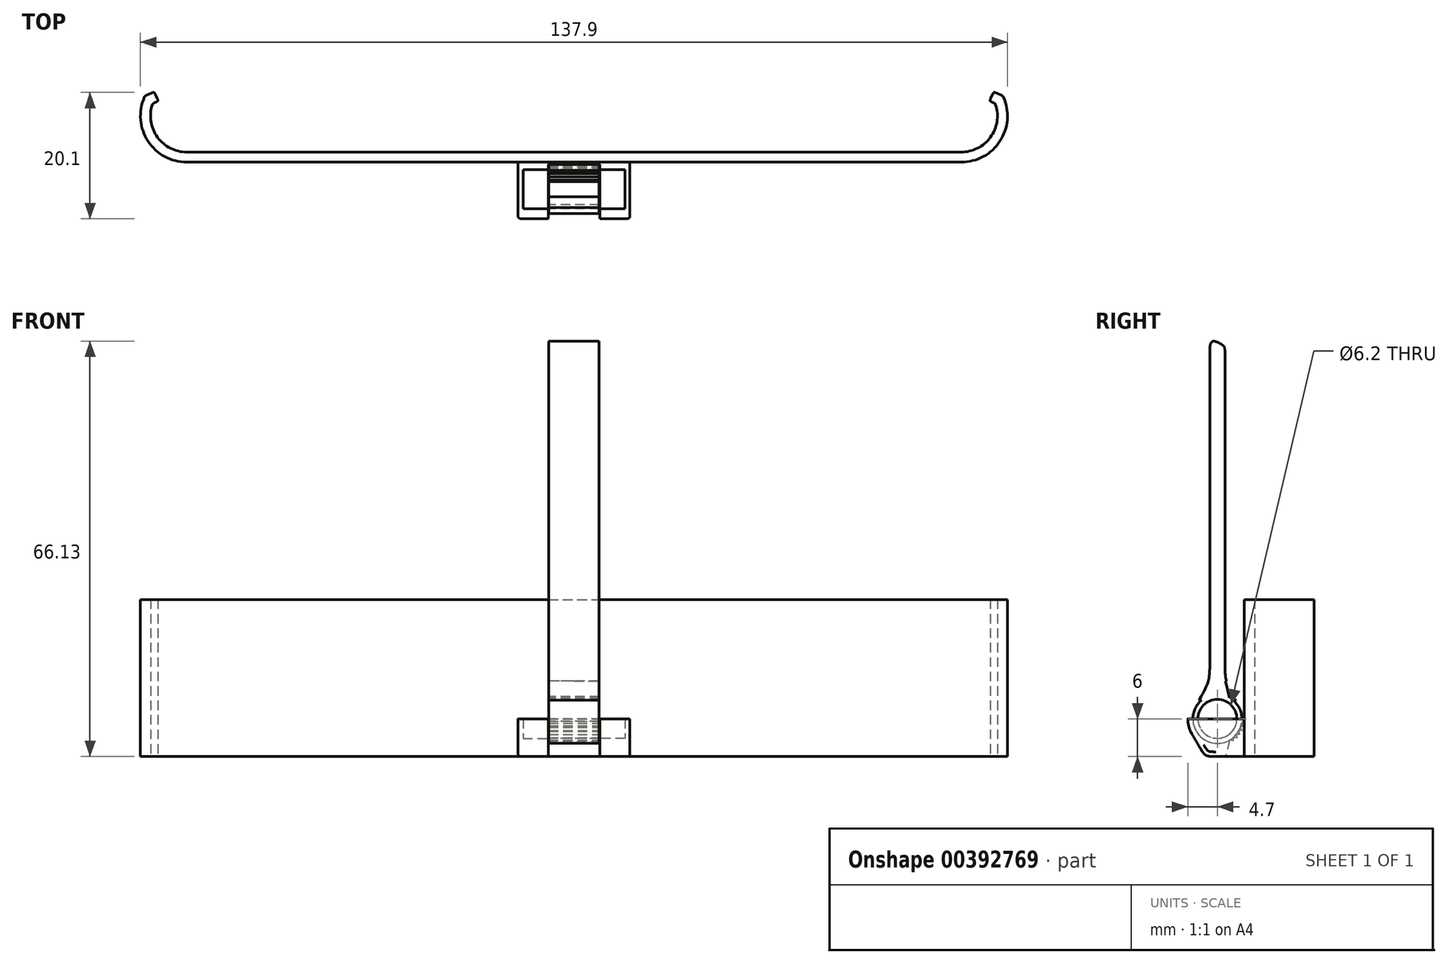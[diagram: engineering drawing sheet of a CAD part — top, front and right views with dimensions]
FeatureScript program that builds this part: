
annotation { "Feature Type Name" : "Feature", "Feature Type Description" : "" }
export const myFeature = defineFeature(function(context is Context, id is Id, definition is map)
    precondition{}
    {
        {
            var Q0;
            Q0=qCreatedBy(makeId("Top.planeOp"),FACE);
            var sketch = newSketch(context, id + "F0", { "sketchPlane" : qUnion([Q0])});
            skLineSegment(sketch, "E0", {"start": v(0, 0) * mm, "end": v(61.6, 0) * mm});
            skLineSegment(sketch, "E1", {"start": v(67, 7.72) * mm, "end": v(66.1, 8.14) * mm});
            skArc(sketch, "E2", {"start": v(61.6, 0) * mm, "mid": v(66.3, 2.45) * mm, "end": v(67, 7.72) * mm});
            skLineSegment(sketch, "E3", {"start": v(61.6, 5.75) * mm, "end": v(67, 7.72) * mm, "construction": true});
            skLineSegment(sketch, "E4", {"start": v(67, 7.72) * mm, "end": v(65.65, 11.43) * mm, "construction": true});
            skLineSegment(sketch, "E5", {"start": v(0, 0) * mm, "end": v(0, -1.6) * mm});
            skLineSegment(sketch, "E6", {"start": v(0, -1.6) * mm, "end": v(61.6, -1.6) * mm});
            skArc(sketch, "E7", {"start": v(61.6, -1.6) * mm, "mid": v(67.81, 1.82) * mm, "end": v(68.23, 8.9) * mm});
            skLineSegment(sketch, "E8", {"start": v(68.23, 8.9) * mm, "end": v(66.77, 9.59) * mm});
            skLineSegment(sketch, "E9", {"start": v(66.77, 9.59) * mm, "end": v(66.1, 8.14) * mm});
            skSolve(sketch);
        }
        {
            var Q0;
            Q0 = qSketchRegion(id + "F0", true);
            extrude(context, id + "F1", {"entities" : qUnion([Q0]), "endBound" : BoundingType.SYMMETRIC, "depth" : 25 * mm});
        }
        {
            var Q0;
            Q0=makeQuery(id+"F1.opExtrude","SWEPT_EDGE",EDGE,{"disambiguationData":[OSD([sQuery(id+"F0.wireOp",EDGE,"E1"),sQuery(id+"F0.wireOp",EDGE,"E2")])]});
            var Q1;
            Q1=makeQuery(id+"F1.opExtrude","SWEPT_EDGE",EDGE,{"disambiguationData":[OSD([sQuery(id+"F0.wireOp",EDGE,"E1"),sQuery(id+"F0.wireOp",EDGE,"E9")])]});
            var Q2;
            Q2=makeQuery(id+"F1.opExtrude","SWEPT_EDGE",EDGE,{"disambiguationData":[OSD([sQuery(id+"F0.wireOp",EDGE,"E8"),sQuery(id+"F0.wireOp",EDGE,"E9")])]});
            var Q3;
            Q3=makeQuery(id+"F1.opExtrude","SWEPT_EDGE",EDGE,{"disambiguationData":[OSD([sQuery(id+"F0.wireOp",EDGE,"E7"),sQuery(id+"F0.wireOp",EDGE,"E8")])]});
            fillet(context, id + "F2", {"entities" : qUnion([Q0, Q1, Q2, Q3]), "radius" : .5 * mm, "tangentPropagation" : true, "rho" : .7, "crossSection" : FilletCrossSection.CONIC, "allowEdgeOverflow" : false});
        }
        {
            var Q0;
            Q0=qCreatedBy(makeId("Right.planeOp"),FACE);
            cPlane(context, id + "F3", {"entities" : qUnion([Q0]), "cplaneType" : CPlaneType.OFFSET, "offset" : 4.1 * mm, "width" : 150 * mm, "height" : 150 * mm});
        }
        {
            var Q0;
            Q0=qCreatedBy(id+"F3.planeOp",FACE);
            var sketch = newSketch(context, id + "F4", { "sketchPlane" : qUnion([Q0])});
            skLineSegment(sketch, "E10", {"start": v(-7.86, -12.5) * mm, "end": v(-9.97, -8.85) * mm});
            skArc(sketch, "E11", {"start": v(-10.6, -6.5) * mm, "mid": v(-10.44, -7.72) * mm, "end": v(-9.97, -8.85) * mm});
            skArc(sketch, "E12", {"start": v(-9, -6.5) * mm, "mid": v(-5.9, -9.6) * mm, "end": v(-2.8, -6.5) * mm});
            skLineSegment(sketch, "E13", {"start": v(-2.8, -6.5) * mm, "end": v(-1.6, -6.5) * mm});
            skLineSegment(sketch, "E14", {"start": v(-1.6, -6.5) * mm, "end": v(-1.6, -12.5) * mm});
            skLineSegment(sketch, "E15", {"start": v(-9, -6.5) * mm, "end": v(-10.6, -6.5) * mm});
            skLineSegment(sketch, "E16", {"start": v(-1.6, -12.5) * mm, "end": v(-7.86, -12.5) * mm});
            skSolve(sketch);
        }
        {
            var Q0;
            Q0 = qSketchRegion(id + "F4", true);
            extrude(context, id + "F5", {"entities" : qUnion([Q0]), "operationType" : NewBodyOperationType.ADD, "depth" : 4 * mm});
        }
        {
            var Q0;
            Q0=makeQuery(id+"F5.opExtrude","CAP_FACE",FACE,{"disambiguationData":[OSD([sQuery(id+"F4.wireOp",EDGE,"pzVoG1jN-wFmN-uIL8-jvUG-rm5sUtAQ56AL"),sQuery(id+"F4.wireOp",EDGE,"E10"),sQuery(id+"F4.wireOp",EDGE,"E11"),sQuery(id+"F4.wireOp",EDGE,"f0MZyzKJ-CONF-h5lc-jCnh-KOTXd5ug3wsI"),sQuery(id+"F4.wireOp",EDGE,"E12"),sQuery(id+"F4.wireOp",EDGE,"E13")])],"isStart":true});
            var sketch = newSketch(context, id + "F6", { "sketchPlane" : qUnion([Q0])});
            skLineSegment(sketch, "E17", {"start": v(1.6, -6.5) * mm, "end": v(1.6, -12.5) * mm});
            skLineSegment(sketch, "E18", {"start": v(1.75, -23.1) * mm, "end": v(1.75, -7.61) * mm, "construction": true});
            skLineSegment(sketch, "E19", {"start": v(1.75, -7.61) * mm, "end": v(2.06, -7.18) * mm});
            skLineSegment(sketch, "E20", {"start": v(2.06, -7.18) * mm, "end": v(1.62, -6.87) * mm});
            skLineSegment(sketch, "E21", {"start": v(1.62, -6.87) * mm, "end": v(2, -6.5) * mm});
            skLineSegment(sketch, "E22", {"start": v(2, -6.5) * mm, "end": v(1.6, -6.5) * mm});
            skCircle(sketch, "E23", {"center": v(5.9, -6.5) * mm, "radius": 4.3 * mm, "construction": true});
            skLineSegment(sketch, "E24", {"start": v(2, -6.5) * mm, "end": v(5.9, -6.5) * mm, "construction": true});
            skCircle(sketch, "E25", {"center": v(5.9, -6.5) * mm, "radius": 3.9 * mm, "construction": true});
            skLineSegment(sketch, "E26", {"start": v(4.62, -12.5) * mm, "end": v(1.6, -12.5) * mm});
            skLineSegment(sketch, "E27", {"start": v(1.6, -12.5) * mm, "end": v(1.6, -6.5) * mm});
            skLineSegment(sketch, "E28", {"start": v(5.9, -6.5) * mm, "end": v(2.06, -7.18) * mm, "construction": true});
            skLineSegment(sketch, "E29", {"start": v(1.75, -7.61) * mm, "end": v(2.24, -7.83) * mm});
            skLineSegment(sketch, "E30", {"start": v(2.24, -7.83) * mm, "end": v(2, -8.32) * mm});
            skLineSegment(sketch, "E31", {"start": v(2, -8.32) * mm, "end": v(2.52, -8.45) * mm});
            skLineSegment(sketch, "E32", {"start": v(2.52, -8.45) * mm, "end": v(2.38, -8.97) * mm});
            skLineSegment(sketch, "E33", {"start": v(2.38, -8.97) * mm, "end": v(2.91, -9) * mm});
            skLineSegment(sketch, "E34", {"start": v(2.91, -9) * mm, "end": v(2.86, -9.54) * mm});
            skLineSegment(sketch, "E35", {"start": v(2.86, -9.54) * mm, "end": v(3.4, -9.49) * mm});
            skLineSegment(sketch, "E36", {"start": v(3.4, -9.49) * mm, "end": v(3.43, -10.02) * mm});
            skLineSegment(sketch, "E37", {"start": v(3.43, -10.02) * mm, "end": v(3.95, -9.88) * mm});
            skLineSegment(sketch, "E38", {"start": v(3.95, -9.88) * mm, "end": v(4.08, -10.4) * mm});
            skLineSegment(sketch, "E39", {"start": v(4.08, -10.4) * mm, "end": v(4.62, -12.5) * mm});
            skSolve(sketch);
        }
        {
            var Q0;
            Q0 = qSketchRegion(id + "F6", true);
            var Q1;
            Q1=qCreatedBy(makeId("Origin.pointOp"),VERTEX);
            extrude(context, id + "F7", {"entities" : qUnion([Q0]), "operationType" : NewBodyOperationType.ADD, "endBound" : BoundingType.UP_TO_VERTEX, "endBoundEntityVertex" : qUnion([Q1]), "depth" : 4 * mm});
        }
        {
            var Q0;
            Q0=makeQuery(id+"F5.opExtrude","CAP_FACE",FACE,{"disambiguationData":[OSD([sQuery(id+"F4.wireOp",EDGE,"E10"),sQuery(id+"F4.wireOp",EDGE,"E11"),sQuery(id+"F4.wireOp",EDGE,"E12"),sQuery(id+"F4.wireOp",EDGE,"E13"),sQuery(id+"F4.wireOp",EDGE,"E14"),sQuery(id+"F4.wireOp",EDGE,"E15"),sQuery(id+"F4.wireOp",EDGE,"E16")])],"isStart":false});
            var sketch = newSketch(context, id + "F8", { "sketchPlane" : qUnion([Q0])});
            skLineSegment(sketch, "E40.0.0", {"start": v(-1.6, -12.5) * mm, "end": v(-1.6, -6.5) * mm});
            skLineSegment(sketch, "E40.0.1", {"start": v(-1.6, -6.5) * mm, "end": v(-2.8, -6.5) * mm});
            skLineSegment(sketch, "E40.0.3", {"start": v(-9, -6.5) * mm, "end": v(-10.6, -6.5) * mm});
            skArc(sketch, "E40.0.4", {"start": v(-10.6, -6.5) * mm, "mid": v(-10.44, -7.72) * mm, "end": v(-9.97, -8.85) * mm});
            skLineSegment(sketch, "E40.0.5", {"start": v(-9.97, -8.85) * mm, "end": v(-7.86, -12.5) * mm});
            skLineSegment(sketch, "E40.0.6", {"start": v(-7.86, -12.5) * mm, "end": v(-1.6, -12.5) * mm});
            skLineSegment(sketch, "E41", {"start": v(-9, -6.5) * mm, "end": v(-2.8, -6.5) * mm});
            skSolve(sketch);
        }
        {
            var Q0;
            Q0 = qSketchRegion(id + "F8", true);
            extrude(context, id + "F9", {"entities" : qUnion([Q0]), "operationType" : NewBodyOperationType.ADD, "depth" : .8 * mm});
        }
        {
            var Q0;
            Q0=qCreatedBy(makeId("Right.planeOp"),FACE);
            var sketch = newSketch(context, id + "F10", { "sketchPlane" : qUnion([Q0])});
            skCircle(sketch, "E42", {"center": v(-5.9, -6.5) * mm, "radius": 3.1 * mm});
            skPoint(sketch, "E43.center", {"position": v(0, -4.1) * mm});
            skCircle(sketch, "E44", {"center": v(-5.9, -6.5) * mm, "radius": 3.9 * mm});
            skSolve(sketch);
        }
        {
            var Q0;
            Q0 = qSketchRegion(id + "F10", true);
            extrude(context, id + "F11", {"entities" : qUnion([Q0]), "depth" : 4 * mm});
        }
        {
            var Q0;
            Q0=qCreatedBy(makeId("Right.planeOp"),FACE);
            var sketch = newSketch(context, id + "F12", { "sketchPlane" : qUnion([Q0])});
            skLineSegment(sketch, "E45", {"start": v(-5.9, -6.5) * mm, "end": v(-2, -6.5) * mm, "construction": true});
            skLineSegment(sketch, "E46", {"start": v(-2, -6.5) * mm, "end": v(-1.73, -6.86) * mm});
            skLineSegment(sketch, "E47", {"start": v(-1.73, -6.86) * mm, "end": v(-2.06, -7.18) * mm});
            skLineSegment(sketch, "E48", {"start": v(-2.06, -7.18) * mm, "end": v(-5.9, -6.5) * mm, "construction": true});
            skLineSegment(sketch, "E49", {"start": v(-2, -6.5) * mm, "end": v(-2.06, -7.18) * mm});
            skSolve(sketch);
        }
        {
            var Q0;
            Q0=makeQuery(id+"F12.imprint","IMPRINT",FACE,{"disambiguationData":[TD([[makeQuery(id+"F12.imprint","IMPRINT",EDGE,{"derivedFrom":sQuery(id+"F12.wireOp",EDGE,"E46")}),-1.0]])]});
            var Q1;
            Q1=makeQuery(id+"F11.opExtrude","CAP_FACE",FACE,{"disambiguationData":[OSD([sQuery(id+"F10.wireOp",EDGE,"E42"),sQuery(id+"F10.wireOp",EDGE,"E44")])],"isStart":false});
            var Q2;
            Q2=makeQuery(id+"F11.opExtrude","SWEPT_BODY",BODY,{"disambiguationData":[OSD([sQuery(id+"F10.wireOp",EDGE,"E42"),sQuery(id+"F10.wireOp",EDGE,"E44")])]});
            var Q3;
            Q3=makeQuery(id+"F11.opExtrude","CAP_FACE",FACE,{"disambiguationData":[OSD([sQuery(id+"F10.wireOp",EDGE,"E42"),sQuery(id+"F10.wireOp",EDGE,"E44")])],"isStart":true});
            extrude(context, id + "F13", {"entities" : qUnion([Q0]), "operationType" : NewBodyOperationType.ADD, "endBound" : BoundingType.UP_TO_SURFACE, "endBoundEntityFace" : qUnion([Q1]), "endBoundEntityBody" : qUnion([Q2]), "depth" : 25 * mm});
        }
        {
            var Q0;
            Q0=makeQuery(id+"F7.boolean.opBoolean","MERGE",FACE,{"derivedFrom":[makeQuery(id+"F5.opExtrude","SWEPT_FACE",FACE,{"disambiguationData":[OSD([sQuery(id+"F4.wireOp",EDGE,"E13")])]}),makeQuery(id+"F7.opExtrude","SWEPT_FACE",FACE,{"disambiguationData":[OSD([sQuery(id+"F6.wireOp",EDGE,"E22")])]})]});
            var sketch = newSketch(context, id + "F14", { "sketchPlane" : qUnion([Q0])});
            skLineSegment(sketch, "E50", {"start": v(4, -5.9) * mm, "end": v(0, -5.9) * mm, "construction": true});
            skSolve(sketch);
        }
        {
            var Q0;
            {var subQ0=sQuery(id+"F12.wireOp",EDGE,"E49");var subQ1=sQuery(id+"F12.wireOp",EDGE,"E47");var subQ2=sQuery(id+"F12.wireOp",EDGE,"E46");Q0=makeQuery(id+"Fb7tVVvyO8J0PkB_2.35.F13.boolean.opBoolean","MERGE",FACE,{"derivedFrom":[makeQuery(id+"Fb7tVVvyO8J0PkB_2.34.F13.boolean.opBoolean","MERGE",FACE,{"derivedFrom":[makeQuery(id+"Fb7tVVvyO8J0PkB_2.33.F13.boolean.opBoolean","MERGE",FACE,{"derivedFrom":[makeQuery(id+"Fb7tVVvyO8J0PkB_2.32.F13.boolean.opBoolean","MERGE",FACE,{"derivedFrom":[makeQuery(id+"Fb7tVVvyO8J0PkB_2.31.F13.boolean.opBoolean","MERGE",FACE,{"derivedFrom":[makeQuery(id+"Fb7tVVvyO8J0PkB_2.30.F13.boolean.opBoolean","MERGE",FACE,{"derivedFrom":[makeQuery(id+"Fb7tVVvyO8J0PkB_2.29.F13.boolean.opBoolean","MERGE",FACE,{"derivedFrom":[makeQuery(id+"Fb7tVVvyO8J0PkB_2.28.F13.boolean.opBoolean","MERGE",FACE,{"derivedFrom":[makeQuery(id+"Fb7tVVvyO8J0PkB_2.27.F13.boolean.opBoolean","MERGE",FACE,{"derivedFrom":[makeQuery(id+"Fb7tVVvyO8J0PkB_2.26.F13.boolean.opBoolean","MERGE",FACE,{"derivedFrom":[makeQuery(id+"Fb7tVVvyO8J0PkB_2.25.F13.boolean.opBoolean","MERGE",FACE,{"derivedFrom":[makeQuery(id+"Fb7tVVvyO8J0PkB_2.24.F13.boolean.opBoolean","MERGE",FACE,{"derivedFrom":[makeQuery(id+"Fb7tVVvyO8J0PkB_2.23.F13.boolean.opBoolean","MERGE",FACE,{"derivedFrom":[makeQuery(id+"Fb7tVVvyO8J0PkB_2.22.F13.boolean.opBoolean","MERGE",FACE,{"derivedFrom":[makeQuery(id+"Fb7tVVvyO8J0PkB_2.21.F13.boolean.opBoolean","MERGE",FACE,{"derivedFrom":[makeQuery(id+"Fb7tVVvyO8J0PkB_2.20.F13.boolean.opBoolean","MERGE",FACE,{"derivedFrom":[makeQuery(id+"Fb7tVVvyO8J0PkB_2.19.F13.boolean.opBoolean","MERGE",FACE,{"derivedFrom":[makeQuery(id+"Fb7tVVvyO8J0PkB_2.18.F13.boolean.opBoolean","MERGE",FACE,{"derivedFrom":[makeQuery(id+"Fb7tVVvyO8J0PkB_2.17.F13.boolean.opBoolean","MERGE",FACE,{"derivedFrom":[makeQuery(id+"Fb7tVVvyO8J0PkB_2.16.F13.boolean.opBoolean","MERGE",FACE,{"derivedFrom":[makeQuery(id+"Fb7tVVvyO8J0PkB_2.15.F13.boolean.opBoolean","MERGE",FACE,{"derivedFrom":[makeQuery(id+"Fb7tVVvyO8J0PkB_2.14.F13.boolean.opBoolean","MERGE",FACE,{"derivedFrom":[makeQuery(id+"Fb7tVVvyO8J0PkB_2.13.F13.boolean.opBoolean","MERGE",FACE,{"derivedFrom":[makeQuery(id+"Fb7tVVvyO8J0PkB_2.12.F13.boolean.opBoolean","MERGE",FACE,{"derivedFrom":[makeQuery(id+"Fb7tVVvyO8J0PkB_2.11.F13.boolean.opBoolean","MERGE",FACE,{"derivedFrom":[makeQuery(id+"Fb7tVVvyO8J0PkB_2.10.F13.boolean.opBoolean","MERGE",FACE,{"derivedFrom":[makeQuery(id+"Fb7tVVvyO8J0PkB_2.9.F13.boolean.opBoolean","MERGE",FACE,{"derivedFrom":[makeQuery(id+"Fb7tVVvyO8J0PkB_2.8.F13.boolean.opBoolean","MERGE",FACE,{"derivedFrom":[makeQuery(id+"Fb7tVVvyO8J0PkB_2.7.F13.boolean.opBoolean","MERGE",FACE,{"derivedFrom":[makeQuery(id+"Fb7tVVvyO8J0PkB_2.6.F13.boolean.opBoolean","MERGE",FACE,{"derivedFrom":[makeQuery(id+"Fb7tVVvyO8J0PkB_2.5.F13.boolean.opBoolean","MERGE",FACE,{"derivedFrom":[makeQuery(id+"Fb7tVVvyO8J0PkB_2.4.F13.boolean.opBoolean","MERGE",FACE,{"derivedFrom":[makeQuery(id+"Fb7tVVvyO8J0PkB_2.3.F13.boolean.opBoolean","MERGE",FACE,{"derivedFrom":[makeQuery(id+"Fb7tVVvyO8J0PkB_2.2.F13.boolean.opBoolean","MERGE",FACE,{"derivedFrom":[makeQuery(id+"Fb7tVVvyO8J0PkB_2.1.F13.boolean.opBoolean","MERGE",FACE,{"derivedFrom":[makeQuery(id+"F13.boolean.opBoolean","MERGE",FACE,{"derivedFrom":[makeQuery(id+"F11.opExtrude","CAP_FACE",FACE,{"disambiguationData":[OSD([sQuery(id+"F10.wireOp",EDGE,"E42"),sQuery(id+"F10.wireOp",EDGE,"E44")])],"isStart":true}),makeQuery(id+"F13.opExtrude","CAP_FACE",FACE,{"disambiguationData":[OSD([subQ2,subQ1,subQ0])],"isStart":true})]}),makeQuery(id+"Fb7tVVvyO8J0PkB_2.1.F13.opExtrude","CAP_FACE",FACE,{"disambiguationData":[OSD([subQ2,subQ1,subQ0])],"isStart":true})]}),makeQuery(id+"Fb7tVVvyO8J0PkB_2.2.F13.opExtrude","CAP_FACE",FACE,{"disambiguationData":[OSD([subQ2,subQ1,subQ0])],"isStart":true})]}),makeQuery(id+"Fb7tVVvyO8J0PkB_2.3.F13.opExtrude","CAP_FACE",FACE,{"disambiguationData":[OSD([subQ2,subQ1,subQ0])],"isStart":true})]}),makeQuery(id+"Fb7tVVvyO8J0PkB_2.4.F13.opExtrude","CAP_FACE",FACE,{"disambiguationData":[OSD([subQ2,subQ1,subQ0])],"isStart":true})]}),makeQuery(id+"Fb7tVVvyO8J0PkB_2.5.F13.opExtrude","CAP_FACE",FACE,{"disambiguationData":[OSD([subQ2,subQ1,subQ0])],"isStart":true})]}),makeQuery(id+"Fb7tVVvyO8J0PkB_2.6.F13.opExtrude","CAP_FACE",FACE,{"disambiguationData":[OSD([subQ2,subQ1,subQ0])],"isStart":true})]}),makeQuery(id+"Fb7tVVvyO8J0PkB_2.7.F13.opExtrude","CAP_FACE",FACE,{"disambiguationData":[OSD([subQ2,subQ1,subQ0])],"isStart":true})]}),makeQuery(id+"Fb7tVVvyO8J0PkB_2.8.F13.opExtrude","CAP_FACE",FACE,{"disambiguationData":[OSD([subQ2,subQ1,subQ0])],"isStart":true})]}),makeQuery(id+"Fb7tVVvyO8J0PkB_2.9.F13.opExtrude","CAP_FACE",FACE,{"disambiguationData":[OSD([subQ2,subQ1,subQ0])],"isStart":true})]}),makeQuery(id+"Fb7tVVvyO8J0PkB_2.10.F13.opExtrude","CAP_FACE",FACE,{"disambiguationData":[OSD([subQ2,subQ1,subQ0])],"isStart":true})]}),makeQuery(id+"Fb7tVVvyO8J0PkB_2.11.F13.opExtrude","CAP_FACE",FACE,{"disambiguationData":[OSD([subQ2,subQ1,subQ0])],"isStart":true})]}),makeQuery(id+"Fb7tVVvyO8J0PkB_2.12.F13.opExtrude","CAP_FACE",FACE,{"disambiguationData":[OSD([subQ2,subQ1,subQ0])],"isStart":true})]}),makeQuery(id+"Fb7tVVvyO8J0PkB_2.13.F13.opExtrude","CAP_FACE",FACE,{"disambiguationData":[OSD([subQ2,subQ1,subQ0])],"isStart":true})]}),makeQuery(id+"Fb7tVVvyO8J0PkB_2.14.F13.opExtrude","CAP_FACE",FACE,{"disambiguationData":[OSD([subQ2,subQ1,subQ0])],"isStart":true})]}),makeQuery(id+"Fb7tVVvyO8J0PkB_2.15.F13.opExtrude","CAP_FACE",FACE,{"disambiguationData":[OSD([subQ2,subQ1,subQ0])],"isStart":true})]}),makeQuery(id+"Fb7tVVvyO8J0PkB_2.16.F13.opExtrude","CAP_FACE",FACE,{"disambiguationData":[OSD([subQ2,subQ1,subQ0])],"isStart":true})]}),makeQuery(id+"Fb7tVVvyO8J0PkB_2.17.F13.opExtrude","CAP_FACE",FACE,{"disambiguationData":[OSD([subQ2,subQ1,subQ0])],"isStart":true})]}),makeQuery(id+"Fb7tVVvyO8J0PkB_2.18.F13.opExtrude","CAP_FACE",FACE,{"disambiguationData":[OSD([subQ2,subQ1,subQ0])],"isStart":true})]}),makeQuery(id+"Fb7tVVvyO8J0PkB_2.19.F13.opExtrude","CAP_FACE",FACE,{"disambiguationData":[OSD([subQ2,subQ1,subQ0])],"isStart":true})]}),makeQuery(id+"Fb7tVVvyO8J0PkB_2.20.F13.opExtrude","CAP_FACE",FACE,{"disambiguationData":[OSD([subQ2,subQ1,subQ0])],"isStart":true})]}),makeQuery(id+"Fb7tVVvyO8J0PkB_2.21.F13.opExtrude","CAP_FACE",FACE,{"disambiguationData":[OSD([subQ2,subQ1,subQ0])],"isStart":true})]}),makeQuery(id+"Fb7tVVvyO8J0PkB_2.22.F13.opExtrude","CAP_FACE",FACE,{"disambiguationData":[OSD([subQ2,subQ1,subQ0])],"isStart":true})]}),makeQuery(id+"Fb7tVVvyO8J0PkB_2.23.F13.opExtrude","CAP_FACE",FACE,{"disambiguationData":[OSD([subQ2,subQ1,subQ0])],"isStart":true})]}),makeQuery(id+"Fb7tVVvyO8J0PkB_2.24.F13.opExtrude","CAP_FACE",FACE,{"disambiguationData":[OSD([subQ2,subQ1,subQ0])],"isStart":true})]}),makeQuery(id+"Fb7tVVvyO8J0PkB_2.25.F13.opExtrude","CAP_FACE",FACE,{"disambiguationData":[OSD([subQ2,subQ1,subQ0])],"isStart":true})]}),makeQuery(id+"Fb7tVVvyO8J0PkB_2.26.F13.opExtrude","CAP_FACE",FACE,{"disambiguationData":[OSD([subQ2,subQ1,subQ0])],"isStart":true})]}),makeQuery(id+"Fb7tVVvyO8J0PkB_2.27.F13.opExtrude","CAP_FACE",FACE,{"disambiguationData":[OSD([subQ2,subQ1,subQ0])],"isStart":true})]}),makeQuery(id+"Fb7tVVvyO8J0PkB_2.28.F13.opExtrude","CAP_FACE",FACE,{"disambiguationData":[OSD([subQ2,subQ1,subQ0])],"isStart":true})]}),makeQuery(id+"Fb7tVVvyO8J0PkB_2.29.F13.opExtrude","CAP_FACE",FACE,{"disambiguationData":[OSD([subQ2,subQ1,subQ0])],"isStart":true})]}),makeQuery(id+"Fb7tVVvyO8J0PkB_2.30.F13.opExtrude","CAP_FACE",FACE,{"disambiguationData":[OSD([subQ2,subQ1,subQ0])],"isStart":true})]}),makeQuery(id+"Fb7tVVvyO8J0PkB_2.31.F13.opExtrude","CAP_FACE",FACE,{"disambiguationData":[OSD([subQ2,subQ1,subQ0])],"isStart":true})]}),makeQuery(id+"Fb7tVVvyO8J0PkB_2.32.F13.opExtrude","CAP_FACE",FACE,{"disambiguationData":[OSD([subQ2,subQ1,subQ0])],"isStart":true})]}),makeQuery(id+"Fb7tVVvyO8J0PkB_2.33.F13.opExtrude","CAP_FACE",FACE,{"disambiguationData":[OSD([subQ2,subQ1,subQ0])],"isStart":true})]}),makeQuery(id+"Fb7tVVvyO8J0PkB_2.34.F13.opExtrude","CAP_FACE",FACE,{"disambiguationData":[OSD([subQ2,subQ1,subQ0])],"isStart":true})]}),makeQuery(id+"Fb7tVVvyO8J0PkB_2.35.F13.opExtrude","CAP_FACE",FACE,{"disambiguationData":[OSD([subQ2,subQ1,subQ0])],"isStart":true})]});}
            var sketch = newSketch(context, id + "F15", { "sketchPlane" : qUnion([Q0])});
            skLineSegment(sketch, "E51", {"start": v(8.86, -9.46) * mm, "end": v(8.89, -9) * mm});
            skLineSegment(sketch, "E52", {"start": v(2.91, -9) * mm, "end": v(2.94, -9.46) * mm});
            skLineSegment(sketch, "E53", {"start": v(5.9, -6.5) * mm, "end": v(5.9, 53.5) * mm, "construction": true});
            skLineSegment(sketch, "E54", {"start": v(7.1, -1.6) * mm, "end": v(7.1, 54.2) * mm});
            skLineSegment(sketch, "E55", {"start": v(7.1, 54.2) * mm, "end": v(4.7, 52.8) * mm});
            skLineSegment(sketch, "E56", {"start": v(4.7, 52.8) * mm, "end": v(4.7, -1.6) * mm});
            skLineSegment(sketch, "E57", {"start": v(7.1, -1.6) * mm, "end": v(8.86, -3.54) * mm});
            skLineSegment(sketch, "E58", {"start": v(2.94, -3.54) * mm, "end": v(4.7, -1.6) * mm});
            skLineSegment(sketch, "E59", {"start": v(4.7, -1.6) * mm, "end": v(7.1, -1.6) * mm, "construction": true});
            skLineSegment(sketch, "E60", {"start": v(2.94, -3.54) * mm, "end": v(3.4, -3.51) * mm});
            skLineSegment(sketch, "E61", {"start": v(8.4, -3.51) * mm, "end": v(8.86, -3.54) * mm});
            skLineSegment(sketch, "E62", {"start": v(3.4, -3.51) * mm, "end": v(5.9, -2.6) * mm});
            skLineSegment(sketch, "E63", {"start": v(5.9, -2.6) * mm, "end": v(8.4, -3.51) * mm});
            skSolve(sketch);
        }
        {
            var Q0;
            Q0 = qSketchRegion(id + "F15", true);
            var Q1;
            {var subQ0=sQuery(id+"F10.wireOp",EDGE,"E44");var subQ1=sQuery(id+"F10.wireOp",EDGE,"E42");Q1=makeQuery(id+"Fb7tVVvyO8J0PkB_2.35.F13.boolean.opBoolean","MERGE",FACE,{"derivedFrom":[makeQuery(id+"Fb7tVVvyO8J0PkB_2.34.F13.boolean.opBoolean","MERGE",FACE,{"derivedFrom":[makeQuery(id+"Fb7tVVvyO8J0PkB_2.33.F13.boolean.opBoolean","MERGE",FACE,{"derivedFrom":[makeQuery(id+"Fb7tVVvyO8J0PkB_2.32.F13.boolean.opBoolean","MERGE",FACE,{"derivedFrom":[makeQuery(id+"Fb7tVVvyO8J0PkB_2.31.F13.boolean.opBoolean","MERGE",FACE,{"derivedFrom":[makeQuery(id+"Fb7tVVvyO8J0PkB_2.30.F13.boolean.opBoolean","MERGE",FACE,{"derivedFrom":[makeQuery(id+"Fb7tVVvyO8J0PkB_2.29.F13.boolean.opBoolean","MERGE",FACE,{"derivedFrom":[makeQuery(id+"Fb7tVVvyO8J0PkB_2.28.F13.boolean.opBoolean","MERGE",FACE,{"derivedFrom":[makeQuery(id+"Fb7tVVvyO8J0PkB_2.27.F13.boolean.opBoolean","MERGE",FACE,{"derivedFrom":[makeQuery(id+"Fb7tVVvyO8J0PkB_2.26.F13.boolean.opBoolean","MERGE",FACE,{"derivedFrom":[makeQuery(id+"Fb7tVVvyO8J0PkB_2.25.F13.boolean.opBoolean","MERGE",FACE,{"derivedFrom":[makeQuery(id+"Fb7tVVvyO8J0PkB_2.24.F13.boolean.opBoolean","MERGE",FACE,{"derivedFrom":[makeQuery(id+"Fb7tVVvyO8J0PkB_2.23.F13.boolean.opBoolean","MERGE",FACE,{"derivedFrom":[makeQuery(id+"Fb7tVVvyO8J0PkB_2.22.F13.boolean.opBoolean","MERGE",FACE,{"derivedFrom":[makeQuery(id+"Fb7tVVvyO8J0PkB_2.21.F13.boolean.opBoolean","MERGE",FACE,{"derivedFrom":[makeQuery(id+"Fb7tVVvyO8J0PkB_2.20.F13.boolean.opBoolean","MERGE",FACE,{"derivedFrom":[makeQuery(id+"Fb7tVVvyO8J0PkB_2.19.F13.boolean.opBoolean","MERGE",FACE,{"derivedFrom":[makeQuery(id+"Fb7tVVvyO8J0PkB_2.18.F13.boolean.opBoolean","MERGE",FACE,{"derivedFrom":[makeQuery(id+"Fb7tVVvyO8J0PkB_2.17.F13.boolean.opBoolean","MERGE",FACE,{"derivedFrom":[makeQuery(id+"Fb7tVVvyO8J0PkB_2.16.F13.boolean.opBoolean","MERGE",FACE,{"derivedFrom":[makeQuery(id+"Fb7tVVvyO8J0PkB_2.15.F13.boolean.opBoolean","MERGE",FACE,{"derivedFrom":[makeQuery(id+"Fb7tVVvyO8J0PkB_2.14.F13.boolean.opBoolean","MERGE",FACE,{"derivedFrom":[makeQuery(id+"Fb7tVVvyO8J0PkB_2.13.F13.boolean.opBoolean","MERGE",FACE,{"derivedFrom":[makeQuery(id+"Fb7tVVvyO8J0PkB_2.12.F13.boolean.opBoolean","MERGE",FACE,{"derivedFrom":[makeQuery(id+"Fb7tVVvyO8J0PkB_2.11.F13.boolean.opBoolean","MERGE",FACE,{"derivedFrom":[makeQuery(id+"Fb7tVVvyO8J0PkB_2.10.F13.boolean.opBoolean","MERGE",FACE,{"derivedFrom":[makeQuery(id+"Fb7tVVvyO8J0PkB_2.9.F13.boolean.opBoolean","MERGE",FACE,{"derivedFrom":[makeQuery(id+"Fb7tVVvyO8J0PkB_2.8.F13.boolean.opBoolean","MERGE",FACE,{"derivedFrom":[makeQuery(id+"Fb7tVVvyO8J0PkB_2.7.F13.boolean.opBoolean","MERGE",FACE,{"derivedFrom":[makeQuery(id+"Fb7tVVvyO8J0PkB_2.6.F13.boolean.opBoolean","MERGE",FACE,{"derivedFrom":[makeQuery(id+"Fb7tVVvyO8J0PkB_2.5.F13.boolean.opBoolean","MERGE",FACE,{"derivedFrom":[makeQuery(id+"Fb7tVVvyO8J0PkB_2.4.F13.boolean.opBoolean","MERGE",FACE,{"derivedFrom":[makeQuery(id+"Fb7tVVvyO8J0PkB_2.3.F13.boolean.opBoolean","MERGE",FACE,{"derivedFrom":[makeQuery(id+"Fb7tVVvyO8J0PkB_2.2.F13.boolean.opBoolean","MERGE",FACE,{"derivedFrom":[makeQuery(id+"Fb7tVVvyO8J0PkB_2.1.F13.boolean.opBoolean","MERGE",FACE,{"derivedFrom":[makeQuery(id+"F13.boolean.opBoolean","MERGE",FACE,{"derivedFrom":[makeQuery(id+"F11.opExtrude","CAP_FACE",FACE,{"disambiguationData":[OSD([subQ1,subQ0])],"isStart":false}),makeQuery(id+"F13.opExtrude","CAP_FACE",FACE,{"disambiguationData":[OSD([subQ1,subQ0])],"isStart":false})]}),makeQuery(id+"Fb7tVVvyO8J0PkB_2.1.F13.opExtrude","CAP_FACE",FACE,{"disambiguationData":[OSD([subQ1,subQ0])],"isStart":false})]}),makeQuery(id+"Fb7tVVvyO8J0PkB_2.2.F13.opExtrude","CAP_FACE",FACE,{"disambiguationData":[OSD([subQ1,subQ0])],"isStart":false})]}),makeQuery(id+"Fb7tVVvyO8J0PkB_2.3.F13.opExtrude","CAP_FACE",FACE,{"disambiguationData":[OSD([subQ1,subQ0])],"isStart":false})]}),makeQuery(id+"Fb7tVVvyO8J0PkB_2.4.F13.opExtrude","CAP_FACE",FACE,{"disambiguationData":[OSD([subQ1,subQ0])],"isStart":false})]}),makeQuery(id+"Fb7tVVvyO8J0PkB_2.5.F13.opExtrude","CAP_FACE",FACE,{"disambiguationData":[OSD([subQ1,subQ0])],"isStart":false})]}),makeQuery(id+"Fb7tVVvyO8J0PkB_2.6.F13.opExtrude","CAP_FACE",FACE,{"disambiguationData":[OSD([subQ1,subQ0])],"isStart":false})]}),makeQuery(id+"Fb7tVVvyO8J0PkB_2.7.F13.opExtrude","CAP_FACE",FACE,{"disambiguationData":[OSD([subQ1,subQ0])],"isStart":false})]}),makeQuery(id+"Fb7tVVvyO8J0PkB_2.8.F13.opExtrude","CAP_FACE",FACE,{"disambiguationData":[OSD([subQ1,subQ0])],"isStart":false})]}),makeQuery(id+"Fb7tVVvyO8J0PkB_2.9.F13.opExtrude","CAP_FACE",FACE,{"disambiguationData":[OSD([subQ1,subQ0])],"isStart":false})]}),makeQuery(id+"Fb7tVVvyO8J0PkB_2.10.F13.opExtrude","CAP_FACE",FACE,{"disambiguationData":[OSD([subQ1,subQ0])],"isStart":false})]}),makeQuery(id+"Fb7tVVvyO8J0PkB_2.11.F13.opExtrude","CAP_FACE",FACE,{"disambiguationData":[OSD([subQ1,subQ0])],"isStart":false})]}),makeQuery(id+"Fb7tVVvyO8J0PkB_2.12.F13.opExtrude","CAP_FACE",FACE,{"disambiguationData":[OSD([subQ1,subQ0])],"isStart":false})]}),makeQuery(id+"Fb7tVVvyO8J0PkB_2.13.F13.opExtrude","CAP_FACE",FACE,{"disambiguationData":[OSD([subQ1,subQ0])],"isStart":false})]}),makeQuery(id+"Fb7tVVvyO8J0PkB_2.14.F13.opExtrude","CAP_FACE",FACE,{"disambiguationData":[OSD([subQ1,subQ0])],"isStart":false})]}),makeQuery(id+"Fb7tVVvyO8J0PkB_2.15.F13.opExtrude","CAP_FACE",FACE,{"disambiguationData":[OSD([subQ1,subQ0])],"isStart":false})]}),makeQuery(id+"Fb7tVVvyO8J0PkB_2.16.F13.opExtrude","CAP_FACE",FACE,{"disambiguationData":[OSD([subQ1,subQ0])],"isStart":false})]}),makeQuery(id+"Fb7tVVvyO8J0PkB_2.17.F13.opExtrude","CAP_FACE",FACE,{"disambiguationData":[OSD([subQ1,subQ0])],"isStart":false})]}),makeQuery(id+"Fb7tVVvyO8J0PkB_2.18.F13.opExtrude","CAP_FACE",FACE,{"disambiguationData":[OSD([subQ1,subQ0])],"isStart":false})]}),makeQuery(id+"Fb7tVVvyO8J0PkB_2.19.F13.opExtrude","CAP_FACE",FACE,{"disambiguationData":[OSD([subQ1,subQ0])],"isStart":false})]}),makeQuery(id+"Fb7tVVvyO8J0PkB_2.20.F13.opExtrude","CAP_FACE",FACE,{"disambiguationData":[OSD([subQ1,subQ0])],"isStart":false})]}),makeQuery(id+"Fb7tVVvyO8J0PkB_2.21.F13.opExtrude","CAP_FACE",FACE,{"disambiguationData":[OSD([subQ1,subQ0])],"isStart":false})]}),makeQuery(id+"Fb7tVVvyO8J0PkB_2.22.F13.opExtrude","CAP_FACE",FACE,{"disambiguationData":[OSD([subQ1,subQ0])],"isStart":false})]}),makeQuery(id+"Fb7tVVvyO8J0PkB_2.23.F13.opExtrude","CAP_FACE",FACE,{"disambiguationData":[OSD([subQ1,subQ0])],"isStart":false})]}),makeQuery(id+"Fb7tVVvyO8J0PkB_2.24.F13.opExtrude","CAP_FACE",FACE,{"disambiguationData":[OSD([subQ1,subQ0])],"isStart":false})]}),makeQuery(id+"Fb7tVVvyO8J0PkB_2.25.F13.opExtrude","CAP_FACE",FACE,{"disambiguationData":[OSD([subQ1,subQ0])],"isStart":false})]}),makeQuery(id+"Fb7tVVvyO8J0PkB_2.26.F13.opExtrude","CAP_FACE",FACE,{"disambiguationData":[OSD([subQ1,subQ0])],"isStart":false})]}),makeQuery(id+"Fb7tVVvyO8J0PkB_2.27.F13.opExtrude","CAP_FACE",FACE,{"disambiguationData":[OSD([subQ1,subQ0])],"isStart":false})]}),makeQuery(id+"Fb7tVVvyO8J0PkB_2.28.F13.opExtrude","CAP_FACE",FACE,{"disambiguationData":[OSD([subQ1,subQ0])],"isStart":false})]}),makeQuery(id+"Fb7tVVvyO8J0PkB_2.29.F13.opExtrude","CAP_FACE",FACE,{"disambiguationData":[OSD([subQ1,subQ0])],"isStart":false})]}),makeQuery(id+"Fb7tVVvyO8J0PkB_2.30.F13.opExtrude","CAP_FACE",FACE,{"disambiguationData":[OSD([subQ1,subQ0])],"isStart":false})]}),makeQuery(id+"Fb7tVVvyO8J0PkB_2.31.F13.opExtrude","CAP_FACE",FACE,{"disambiguationData":[OSD([subQ1,subQ0])],"isStart":false})]}),makeQuery(id+"Fb7tVVvyO8J0PkB_2.32.F13.opExtrude","CAP_FACE",FACE,{"disambiguationData":[OSD([subQ1,subQ0])],"isStart":false})]}),makeQuery(id+"Fb7tVVvyO8J0PkB_2.33.F13.opExtrude","CAP_FACE",FACE,{"disambiguationData":[OSD([subQ1,subQ0])],"isStart":false})]}),makeQuery(id+"Fb7tVVvyO8J0PkB_2.34.F13.opExtrude","CAP_FACE",FACE,{"disambiguationData":[OSD([subQ1,subQ0])],"isStart":false})]}),makeQuery(id+"Fb7tVVvyO8J0PkB_2.35.F13.opExtrude","CAP_FACE",FACE,{"disambiguationData":[OSD([subQ1,subQ0])],"isStart":false})]});}
            extrude(context, id + "F16", {"entities" : qUnion([Q0]), "operationType" : NewBodyOperationType.ADD, "endBound" : BoundingType.UP_TO_SURFACE, "oppositeDirection" : true, "endBoundEntityFace" : qUnion([Q1]), "depth" : 25 * mm});
        }
        {
            var Q0;
            Q0=makeQuery(id+"F16.opExtrude","SWEPT_EDGE",EDGE,{"disambiguationData":[OSD([sQuery(id+"F15.wireOp",EDGE,"E56"),sQuery(id+"F15.wireOp",EDGE,"E58")])]});
            var Q1;
            Q1=makeQuery(id+"F16.opExtrude","SWEPT_EDGE",EDGE,{"disambiguationData":[OSD([sQuery(id+"F15.wireOp",EDGE,"E54"),sQuery(id+"F15.wireOp",EDGE,"E57")])]});
            fillet(context, id + "F17", {"entities" : qUnion([Q0, Q1]), "radius" : 12 * mm, "tangentPropagation" : true, "rho" : .7, "crossSection" : FilletCrossSection.CONIC, "allowEdgeOverflow" : false});
        }
        {
            var Q0;
            Q0 = qSketchRegion(id + "F15", true);
            var Q1;
            {var subQ0=sQuery(id+"F10.wireOp",EDGE,"E44");var subQ1=sQuery(id+"F10.wireOp",EDGE,"E42");Q1=makeQuery(id+"F16.boolean.opBoolean","MERGE",FACE,{"derivedFrom":[makeQuery(id+"Fb7tVVvyO8J0PkB_2.35.F13.boolean.opBoolean","MERGE",FACE,{"derivedFrom":[makeQuery(id+"Fb7tVVvyO8J0PkB_2.34.F13.boolean.opBoolean","MERGE",FACE,{"derivedFrom":[makeQuery(id+"Fb7tVVvyO8J0PkB_2.33.F13.boolean.opBoolean","MERGE",FACE,{"derivedFrom":[makeQuery(id+"Fb7tVVvyO8J0PkB_2.32.F13.boolean.opBoolean","MERGE",FACE,{"derivedFrom":[makeQuery(id+"Fb7tVVvyO8J0PkB_2.31.F13.boolean.opBoolean","MERGE",FACE,{"derivedFrom":[makeQuery(id+"Fb7tVVvyO8J0PkB_2.30.F13.boolean.opBoolean","MERGE",FACE,{"derivedFrom":[makeQuery(id+"Fb7tVVvyO8J0PkB_2.29.F13.boolean.opBoolean","MERGE",FACE,{"derivedFrom":[makeQuery(id+"Fb7tVVvyO8J0PkB_2.28.F13.boolean.opBoolean","MERGE",FACE,{"derivedFrom":[makeQuery(id+"Fb7tVVvyO8J0PkB_2.27.F13.boolean.opBoolean","MERGE",FACE,{"derivedFrom":[makeQuery(id+"Fb7tVVvyO8J0PkB_2.26.F13.boolean.opBoolean","MERGE",FACE,{"derivedFrom":[makeQuery(id+"Fb7tVVvyO8J0PkB_2.25.F13.boolean.opBoolean","MERGE",FACE,{"derivedFrom":[makeQuery(id+"Fb7tVVvyO8J0PkB_2.24.F13.boolean.opBoolean","MERGE",FACE,{"derivedFrom":[makeQuery(id+"Fb7tVVvyO8J0PkB_2.23.F13.boolean.opBoolean","MERGE",FACE,{"derivedFrom":[makeQuery(id+"Fb7tVVvyO8J0PkB_2.22.F13.boolean.opBoolean","MERGE",FACE,{"derivedFrom":[makeQuery(id+"Fb7tVVvyO8J0PkB_2.21.F13.boolean.opBoolean","MERGE",FACE,{"derivedFrom":[makeQuery(id+"Fb7tVVvyO8J0PkB_2.20.F13.boolean.opBoolean","MERGE",FACE,{"derivedFrom":[makeQuery(id+"Fb7tVVvyO8J0PkB_2.19.F13.boolean.opBoolean","MERGE",FACE,{"derivedFrom":[makeQuery(id+"Fb7tVVvyO8J0PkB_2.18.F13.boolean.opBoolean","MERGE",FACE,{"derivedFrom":[makeQuery(id+"Fb7tVVvyO8J0PkB_2.17.F13.boolean.opBoolean","MERGE",FACE,{"derivedFrom":[makeQuery(id+"Fb7tVVvyO8J0PkB_2.16.F13.boolean.opBoolean","MERGE",FACE,{"derivedFrom":[makeQuery(id+"Fb7tVVvyO8J0PkB_2.15.F13.boolean.opBoolean","MERGE",FACE,{"derivedFrom":[makeQuery(id+"Fb7tVVvyO8J0PkB_2.14.F13.boolean.opBoolean","MERGE",FACE,{"derivedFrom":[makeQuery(id+"Fb7tVVvyO8J0PkB_2.13.F13.boolean.opBoolean","MERGE",FACE,{"derivedFrom":[makeQuery(id+"Fb7tVVvyO8J0PkB_2.12.F13.boolean.opBoolean","MERGE",FACE,{"derivedFrom":[makeQuery(id+"Fb7tVVvyO8J0PkB_2.11.F13.boolean.opBoolean","MERGE",FACE,{"derivedFrom":[makeQuery(id+"Fb7tVVvyO8J0PkB_2.10.F13.boolean.opBoolean","MERGE",FACE,{"derivedFrom":[makeQuery(id+"Fb7tVVvyO8J0PkB_2.9.F13.boolean.opBoolean","MERGE",FACE,{"derivedFrom":[makeQuery(id+"Fb7tVVvyO8J0PkB_2.8.F13.boolean.opBoolean","MERGE",FACE,{"derivedFrom":[makeQuery(id+"Fb7tVVvyO8J0PkB_2.7.F13.boolean.opBoolean","MERGE",FACE,{"derivedFrom":[makeQuery(id+"Fb7tVVvyO8J0PkB_2.6.F13.boolean.opBoolean","MERGE",FACE,{"derivedFrom":[makeQuery(id+"Fb7tVVvyO8J0PkB_2.5.F13.boolean.opBoolean","MERGE",FACE,{"derivedFrom":[makeQuery(id+"Fb7tVVvyO8J0PkB_2.4.F13.boolean.opBoolean","MERGE",FACE,{"derivedFrom":[makeQuery(id+"Fb7tVVvyO8J0PkB_2.3.F13.boolean.opBoolean","MERGE",FACE,{"derivedFrom":[makeQuery(id+"Fb7tVVvyO8J0PkB_2.2.F13.boolean.opBoolean","MERGE",FACE,{"derivedFrom":[makeQuery(id+"Fb7tVVvyO8J0PkB_2.1.F13.boolean.opBoolean","MERGE",FACE,{"derivedFrom":[makeQuery(id+"F13.boolean.opBoolean","MERGE",FACE,{"derivedFrom":[makeQuery(id+"F11.opExtrude","CAP_FACE",FACE,{"disambiguationData":[OSD([subQ1,subQ0])],"isStart":false}),makeQuery(id+"F13.opExtrude","CAP_FACE",FACE,{"disambiguationData":[OSD([subQ1,subQ0])],"isStart":false})]}),makeQuery(id+"Fb7tVVvyO8J0PkB_2.1.F13.opExtrude","CAP_FACE",FACE,{"disambiguationData":[OSD([subQ1,subQ0])],"isStart":false})]}),makeQuery(id+"Fb7tVVvyO8J0PkB_2.2.F13.opExtrude","CAP_FACE",FACE,{"disambiguationData":[OSD([subQ1,subQ0])],"isStart":false})]}),makeQuery(id+"Fb7tVVvyO8J0PkB_2.3.F13.opExtrude","CAP_FACE",FACE,{"disambiguationData":[OSD([subQ1,subQ0])],"isStart":false})]}),makeQuery(id+"Fb7tVVvyO8J0PkB_2.4.F13.opExtrude","CAP_FACE",FACE,{"disambiguationData":[OSD([subQ1,subQ0])],"isStart":false})]}),makeQuery(id+"Fb7tVVvyO8J0PkB_2.5.F13.opExtrude","CAP_FACE",FACE,{"disambiguationData":[OSD([subQ1,subQ0])],"isStart":false})]}),makeQuery(id+"Fb7tVVvyO8J0PkB_2.6.F13.opExtrude","CAP_FACE",FACE,{"disambiguationData":[OSD([subQ1,subQ0])],"isStart":false})]}),makeQuery(id+"Fb7tVVvyO8J0PkB_2.7.F13.opExtrude","CAP_FACE",FACE,{"disambiguationData":[OSD([subQ1,subQ0])],"isStart":false})]}),makeQuery(id+"Fb7tVVvyO8J0PkB_2.8.F13.opExtrude","CAP_FACE",FACE,{"disambiguationData":[OSD([subQ1,subQ0])],"isStart":false})]}),makeQuery(id+"Fb7tVVvyO8J0PkB_2.9.F13.opExtrude","CAP_FACE",FACE,{"disambiguationData":[OSD([subQ1,subQ0])],"isStart":false})]}),makeQuery(id+"Fb7tVVvyO8J0PkB_2.10.F13.opExtrude","CAP_FACE",FACE,{"disambiguationData":[OSD([subQ1,subQ0])],"isStart":false})]}),makeQuery(id+"Fb7tVVvyO8J0PkB_2.11.F13.opExtrude","CAP_FACE",FACE,{"disambiguationData":[OSD([subQ1,subQ0])],"isStart":false})]}),makeQuery(id+"Fb7tVVvyO8J0PkB_2.12.F13.opExtrude","CAP_FACE",FACE,{"disambiguationData":[OSD([subQ1,subQ0])],"isStart":false})]}),makeQuery(id+"Fb7tVVvyO8J0PkB_2.13.F13.opExtrude","CAP_FACE",FACE,{"disambiguationData":[OSD([subQ1,subQ0])],"isStart":false})]}),makeQuery(id+"Fb7tVVvyO8J0PkB_2.14.F13.opExtrude","CAP_FACE",FACE,{"disambiguationData":[OSD([subQ1,subQ0])],"isStart":false})]}),makeQuery(id+"Fb7tVVvyO8J0PkB_2.15.F13.opExtrude","CAP_FACE",FACE,{"disambiguationData":[OSD([subQ1,subQ0])],"isStart":false})]}),makeQuery(id+"Fb7tVVvyO8J0PkB_2.16.F13.opExtrude","CAP_FACE",FACE,{"disambiguationData":[OSD([subQ1,subQ0])],"isStart":false})]}),makeQuery(id+"Fb7tVVvyO8J0PkB_2.17.F13.opExtrude","CAP_FACE",FACE,{"disambiguationData":[OSD([subQ1,subQ0])],"isStart":false})]}),makeQuery(id+"Fb7tVVvyO8J0PkB_2.18.F13.opExtrude","CAP_FACE",FACE,{"disambiguationData":[OSD([subQ1,subQ0])],"isStart":false})]}),makeQuery(id+"Fb7tVVvyO8J0PkB_2.19.F13.opExtrude","CAP_FACE",FACE,{"disambiguationData":[OSD([subQ1,subQ0])],"isStart":false})]}),makeQuery(id+"Fb7tVVvyO8J0PkB_2.20.F13.opExtrude","CAP_FACE",FACE,{"disambiguationData":[OSD([subQ1,subQ0])],"isStart":false})]}),makeQuery(id+"Fb7tVVvyO8J0PkB_2.21.F13.opExtrude","CAP_FACE",FACE,{"disambiguationData":[OSD([subQ1,subQ0])],"isStart":false})]}),makeQuery(id+"Fb7tVVvyO8J0PkB_2.22.F13.opExtrude","CAP_FACE",FACE,{"disambiguationData":[OSD([subQ1,subQ0])],"isStart":false})]}),makeQuery(id+"Fb7tVVvyO8J0PkB_2.23.F13.opExtrude","CAP_FACE",FACE,{"disambiguationData":[OSD([subQ1,subQ0])],"isStart":false})]}),makeQuery(id+"Fb7tVVvyO8J0PkB_2.24.F13.opExtrude","CAP_FACE",FACE,{"disambiguationData":[OSD([subQ1,subQ0])],"isStart":false})]}),makeQuery(id+"Fb7tVVvyO8J0PkB_2.25.F13.opExtrude","CAP_FACE",FACE,{"disambiguationData":[OSD([subQ1,subQ0])],"isStart":false})]}),makeQuery(id+"Fb7tVVvyO8J0PkB_2.26.F13.opExtrude","CAP_FACE",FACE,{"disambiguationData":[OSD([subQ1,subQ0])],"isStart":false})]}),makeQuery(id+"Fb7tVVvyO8J0PkB_2.27.F13.opExtrude","CAP_FACE",FACE,{"disambiguationData":[OSD([subQ1,subQ0])],"isStart":false})]}),makeQuery(id+"Fb7tVVvyO8J0PkB_2.28.F13.opExtrude","CAP_FACE",FACE,{"disambiguationData":[OSD([subQ1,subQ0])],"isStart":false})]}),makeQuery(id+"Fb7tVVvyO8J0PkB_2.29.F13.opExtrude","CAP_FACE",FACE,{"disambiguationData":[OSD([subQ1,subQ0])],"isStart":false})]}),makeQuery(id+"Fb7tVVvyO8J0PkB_2.30.F13.opExtrude","CAP_FACE",FACE,{"disambiguationData":[OSD([subQ1,subQ0])],"isStart":false})]}),makeQuery(id+"Fb7tVVvyO8J0PkB_2.31.F13.opExtrude","CAP_FACE",FACE,{"disambiguationData":[OSD([subQ1,subQ0])],"isStart":false})]}),makeQuery(id+"Fb7tVVvyO8J0PkB_2.32.F13.opExtrude","CAP_FACE",FACE,{"disambiguationData":[OSD([subQ1,subQ0])],"isStart":false})]}),makeQuery(id+"Fb7tVVvyO8J0PkB_2.33.F13.opExtrude","CAP_FACE",FACE,{"disambiguationData":[OSD([subQ1,subQ0])],"isStart":false})]}),makeQuery(id+"Fb7tVVvyO8J0PkB_2.34.F13.opExtrude","CAP_FACE",FACE,{"disambiguationData":[OSD([subQ1,subQ0])],"isStart":false})]}),makeQuery(id+"Fb7tVVvyO8J0PkB_2.35.F13.opExtrude","CAP_FACE",FACE,{"disambiguationData":[OSD([subQ1,subQ0])],"isStart":false})]}),makeQuery(id+"F16.opExtrude","CAP_FACE",FACE,{"disambiguationData":[OSD([subQ1,subQ0])],"isStart":false})]});}
            extrude(context, id + "F18", {"entities" : qUnion([Q0]), "operationType" : NewBodyOperationType.ADD, "endBound" : BoundingType.UP_TO_SURFACE, "oppositeDirection" : true, "endBoundEntityFace" : qUnion([Q1]), "depth" : 25 * mm});
        }
        {
            var Q0;
            Q0=makeQuery(id+"F6QAZeA2A2lZs83_1.1.F7.boolean.opBoolean","MERGE",FACE,{"derivedFrom":[makeQuery(id+"F7.boolean.opBoolean","MERGE",FACE,{"derivedFrom":[makeQuery(id+"F1.opExtrude","SWEPT_FACE",FACE,{"disambiguationData":[OSD([sQuery(id+"F0.wireOp",EDGE,"E5")])]}),makeQuery(id+"F7.opExtrude","CAP_FACE",FACE,{"disambiguationData":[OSD([dummyQuery(id+"F7.vertexPlane.planeOp",FACE)])],"isStart":false})]}),makeQuery(id+"F6QAZeA2A2lZs83_1.1.F7.opExtrude","CAP_FACE",FACE,{"disambiguationData":[OSD([dummyQuery(id+"F6QAZeA2A2lZs83_1.1.F7.vertexPlane.planeOp",FACE)])],"isStart":false})]});
            var sketch = newSketch(context, id + "F19", { "sketchPlane" : qUnion([Q0])});
            skLineSegment(sketch, "E64", {"start": v(4.62, -0.5) * mm, "end": v(1.6, -0.5) * mm});
            skLineSegment(sketch, "E65", {"start": v(1.6, -0.5) * mm, "end": v(1.6, -1.26) * mm});
            skLineSegment(sketch, "E66", {"start": v(2.86, -3.46) * mm, "end": v(3.4, -3.51) * mm});
            skLineSegment(sketch, "E67", {"start": v(3.4, -3.51) * mm, "end": v(3.43, -2.98) * mm});
            skLineSegment(sketch, "E68", {"start": v(3.43, -2.98) * mm, "end": v(3.95, -3.12) * mm});
            skLineSegment(sketch, "E69", {"start": v(3.95, -3.12) * mm, "end": v(4.62, -0.5) * mm});
            skLineSegment(sketch, "E70", {"start": v(2.86, -3.46) * mm, "end": v(2.91, -4) * mm});
            skLineSegment(sketch, "E71", {"start": v(2.91, -4) * mm, "end": v(2.38, -4.03) * mm});
            skLineSegment(sketch, "E72", {"start": v(2.38, -4.03) * mm, "end": v(1.6, -1.26) * mm});
            skSolve(sketch);
        }
        {
            var Q0;
            Q0 = qSketchRegion(id + "F19", true);
            var Q1;
            {var subQ0=sQuery(id+"F4.wireOp",EDGE,"E16");var subQ1=sQuery(id+"F4.wireOp",EDGE,"E15");var subQ2=sQuery(id+"F4.wireOp",EDGE,"E14");var subQ3=sQuery(id+"F4.wireOp",EDGE,"E13");var subQ4=sQuery(id+"F4.wireOp",EDGE,"E12");var subQ5=sQuery(id+"F4.wireOp",EDGE,"E11");var subQ6=sQuery(id+"F4.wireOp",EDGE,"E10");Q1=makeQuery(id+"F6QAZeA2A2lZs83_1.1.F5.boolean.opBoolean","MERGE",FACE,{"derivedFrom":[makeQuery(id+"F5.opExtrude","CAP_FACE",FACE,{"disambiguationData":[OSD([subQ6,subQ5,subQ4,subQ3,subQ2,subQ1,subQ0])],"isStart":true}),makeQuery(id+"F6QAZeA2A2lZs83_1.1.F5.opExtrude","CAP_FACE",FACE,{"disambiguationData":[OSD([subQ6,subQ5,subQ4,subQ3,subQ2,subQ1,subQ0])],"isStart":true})]});}
            extrude(context, id + "F20", {"entities" : qUnion([Q0]), "operationType" : NewBodyOperationType.REMOVE, "endBound" : BoundingType.UP_TO_SURFACE, "oppositeDirection" : true, "endBoundEntityFace" : qUnion([Q1]), "depth" : 25 * mm});
        }
        {
            var Q0;
            Q0=makeQuery(id+"F5.opExtrude","SWEPT_EDGE",EDGE,{"disambiguationData":[OSD([sQuery(id+"F4.wireOp",EDGE,"E10"),sQuery(id+"F4.wireOp",EDGE,"E16")])]});
            var Q1;
            Q1=makeQuery(id+"F6QAZeA2A2lZs83_1.1.F9.boolean.opBoolean","MERGE",EDGE,{"derivedFrom":[makeQuery(id+"F6QAZeA2A2lZs83_1.1.F5.opExtrude","SWEPT_EDGE",EDGE,{"disambiguationData":[OSD([sQuery(id+"F4.wireOp",EDGE,"E10"),sQuery(id+"F4.wireOp",EDGE,"E16")])]}),makeQuery(id+"F6QAZeA2A2lZs83_1.1.F9.opExtrude","SWEPT_EDGE",EDGE,{"disambiguationData":[OSD([sQuery(id+"F8.wireOp",EDGE,"E40.0.5"),sQuery(id+"F8.wireOp",EDGE,"E40.0.6")])]})]});
            fillet(context, id + "F21", {"entities" : qUnion([Q0, Q1]), "radius" : 3 * mm, "tangentPropagation" : true, "rho" : .7, "crossSection" : FilletCrossSection.CONIC, "allowEdgeOverflow" : false});
        }
        {
            var Q0;
            Q0=makeQuery(id+"F1.opExtrude","SWEPT_BODY",BODY,{"disambiguationData":[OSD([sQuery(id+"F0.wireOp",EDGE,"E0"),sQuery(id+"F0.wireOp",EDGE,"E1"),sQuery(id+"F0.wireOp",EDGE,"E2"),sQuery(id+"F0.wireOp",EDGE,"E5"),sQuery(id+"F0.wireOp",EDGE,"E6"),sQuery(id+"F0.wireOp",EDGE,"E7"),sQuery(id+"F0.wireOp",EDGE,"E8"),sQuery(id+"F0.wireOp",EDGE,"E9")])]});
            var Q1;
            Q1=qCreatedBy(makeId("Right.planeOp"),FACE);
            mirror(context, id + "F22", {"operationType" : NewBodyOperationType.ADD, "entities" : qUnion([Q0]), "mirrorPlane" : qUnion([Q1])});
        }
        {
            var Q0;
            {var subQ0=sQuery(id+"F4.wireOp",EDGE,"E11");Q0=makeQuery(id+"F6QAZeA2A2lZs83_1.1.F5.boolean.opBoolean","MERGE",EDGE,{"derivedFrom":[makeQuery(id+"F5.opExtrude","CAP_EDGE",EDGE,{"disambiguationData":[OSD([subQ0])],"isStart":false}),makeQuery(id+"F6QAZeA2A2lZs83_1.1.F5.opExtrude","CAP_EDGE",EDGE,{"disambiguationData":[OSD([subQ0])],"isStart":false})]});}
            var Q1;
            {var subQ0=sQuery(id+"F4.wireOp",EDGE,"E11");Q1=makeQuery(id+"F22.opPattern","COPY",EDGE,{"derivedFrom":makeQuery(id+"F6QAZeA2A2lZs83_1.1.F5.boolean.opBoolean","MERGE",EDGE,{"derivedFrom":[makeQuery(id+"F5.opExtrude","CAP_EDGE",EDGE,{"disambiguationData":[OSD([subQ0])],"isStart":false}),makeQuery(id+"F6QAZeA2A2lZs83_1.1.F5.opExtrude","CAP_EDGE",EDGE,{"disambiguationData":[OSD([subQ0])],"isStart":false})]}),"instanceName":"1"});}
            var Q2;
            {var subQ0=sQuery(id+"F8.wireOp",EDGE,"E40.0.4");Q2=makeQuery(id+"F22.opPattern","COPY",EDGE,{"derivedFrom":makeQuery(id+"F6QAZeA2A2lZs83_1.1.F9.boolean.opBoolean","MERGE",EDGE,{"derivedFrom":[makeQuery(id+"F9.opExtrude","CAP_EDGE",EDGE,{"disambiguationData":[OSD([subQ0])],"isStart":false}),makeQuery(id+"F6QAZeA2A2lZs83_1.1.F9.opExtrude","CAP_EDGE",EDGE,{"disambiguationData":[OSD([subQ0])],"isStart":false})]}),"instanceName":"1"});}
            var Q3;
            {var subQ0=sQuery(id+"F8.wireOp",EDGE,"E40.0.4");Q3=makeQuery(id+"F6QAZeA2A2lZs83_1.1.F9.boolean.opBoolean","MERGE",EDGE,{"derivedFrom":[makeQuery(id+"F9.opExtrude","CAP_EDGE",EDGE,{"disambiguationData":[OSD([subQ0])],"isStart":false}),makeQuery(id+"F6QAZeA2A2lZs83_1.1.F9.opExtrude","CAP_EDGE",EDGE,{"disambiguationData":[OSD([subQ0])],"isStart":false})]});}
            fillet(context, id + "F23", {"entities" : qUnion([Q0, Q1, Q2, Q3]), "radius" : .75 * mm, "tangentPropagation" : true, "rho" : .7, "crossSection" : FilletCrossSection.CONIC, "allowEdgeOverflow" : false});
        }
        {
            var Q0;
            Q0=makeQuery(id+"F11.opExtrude","SWEPT_BODY",BODY,{"disambiguationData":[OSD([sQuery(id+"F10.wireOp",EDGE,"E42"),sQuery(id+"F10.wireOp",EDGE,"E44")])]});
            var Q1;
            {var subQ0=sQuery(id+"F12.wireOp",EDGE,"E49");var subQ1=sQuery(id+"F12.wireOp",EDGE,"E47");var subQ2=sQuery(id+"F12.wireOp",EDGE,"E46");Q1=makeQuery(id+"F16.boolean.opBoolean","MERGE",FACE,{"derivedFrom":[makeQuery(id+"Fb7tVVvyO8J0PkB_2.35.F13.boolean.opBoolean","MERGE",FACE,{"derivedFrom":[makeQuery(id+"Fb7tVVvyO8J0PkB_2.34.F13.boolean.opBoolean","MERGE",FACE,{"derivedFrom":[makeQuery(id+"Fb7tVVvyO8J0PkB_2.33.F13.boolean.opBoolean","MERGE",FACE,{"derivedFrom":[makeQuery(id+"Fb7tVVvyO8J0PkB_2.32.F13.boolean.opBoolean","MERGE",FACE,{"derivedFrom":[makeQuery(id+"Fb7tVVvyO8J0PkB_2.31.F13.boolean.opBoolean","MERGE",FACE,{"derivedFrom":[makeQuery(id+"Fb7tVVvyO8J0PkB_2.30.F13.boolean.opBoolean","MERGE",FACE,{"derivedFrom":[makeQuery(id+"Fb7tVVvyO8J0PkB_2.29.F13.boolean.opBoolean","MERGE",FACE,{"derivedFrom":[makeQuery(id+"Fb7tVVvyO8J0PkB_2.28.F13.boolean.opBoolean","MERGE",FACE,{"derivedFrom":[makeQuery(id+"Fb7tVVvyO8J0PkB_2.27.F13.boolean.opBoolean","MERGE",FACE,{"derivedFrom":[makeQuery(id+"Fb7tVVvyO8J0PkB_2.26.F13.boolean.opBoolean","MERGE",FACE,{"derivedFrom":[makeQuery(id+"Fb7tVVvyO8J0PkB_2.25.F13.boolean.opBoolean","MERGE",FACE,{"derivedFrom":[makeQuery(id+"Fb7tVVvyO8J0PkB_2.24.F13.boolean.opBoolean","MERGE",FACE,{"derivedFrom":[makeQuery(id+"Fb7tVVvyO8J0PkB_2.23.F13.boolean.opBoolean","MERGE",FACE,{"derivedFrom":[makeQuery(id+"Fb7tVVvyO8J0PkB_2.22.F13.boolean.opBoolean","MERGE",FACE,{"derivedFrom":[makeQuery(id+"Fb7tVVvyO8J0PkB_2.21.F13.boolean.opBoolean","MERGE",FACE,{"derivedFrom":[makeQuery(id+"Fb7tVVvyO8J0PkB_2.20.F13.boolean.opBoolean","MERGE",FACE,{"derivedFrom":[makeQuery(id+"Fb7tVVvyO8J0PkB_2.19.F13.boolean.opBoolean","MERGE",FACE,{"derivedFrom":[makeQuery(id+"Fb7tVVvyO8J0PkB_2.18.F13.boolean.opBoolean","MERGE",FACE,{"derivedFrom":[makeQuery(id+"Fb7tVVvyO8J0PkB_2.17.F13.boolean.opBoolean","MERGE",FACE,{"derivedFrom":[makeQuery(id+"Fb7tVVvyO8J0PkB_2.16.F13.boolean.opBoolean","MERGE",FACE,{"derivedFrom":[makeQuery(id+"Fb7tVVvyO8J0PkB_2.15.F13.boolean.opBoolean","MERGE",FACE,{"derivedFrom":[makeQuery(id+"Fb7tVVvyO8J0PkB_2.14.F13.boolean.opBoolean","MERGE",FACE,{"derivedFrom":[makeQuery(id+"Fb7tVVvyO8J0PkB_2.13.F13.boolean.opBoolean","MERGE",FACE,{"derivedFrom":[makeQuery(id+"Fb7tVVvyO8J0PkB_2.12.F13.boolean.opBoolean","MERGE",FACE,{"derivedFrom":[makeQuery(id+"Fb7tVVvyO8J0PkB_2.11.F13.boolean.opBoolean","MERGE",FACE,{"derivedFrom":[makeQuery(id+"Fb7tVVvyO8J0PkB_2.10.F13.boolean.opBoolean","MERGE",FACE,{"derivedFrom":[makeQuery(id+"Fb7tVVvyO8J0PkB_2.9.F13.boolean.opBoolean","MERGE",FACE,{"derivedFrom":[makeQuery(id+"Fb7tVVvyO8J0PkB_2.8.F13.boolean.opBoolean","MERGE",FACE,{"derivedFrom":[makeQuery(id+"Fb7tVVvyO8J0PkB_2.7.F13.boolean.opBoolean","MERGE",FACE,{"derivedFrom":[makeQuery(id+"Fb7tVVvyO8J0PkB_2.6.F13.boolean.opBoolean","MERGE",FACE,{"derivedFrom":[makeQuery(id+"Fb7tVVvyO8J0PkB_2.5.F13.boolean.opBoolean","MERGE",FACE,{"derivedFrom":[makeQuery(id+"Fb7tVVvyO8J0PkB_2.4.F13.boolean.opBoolean","MERGE",FACE,{"derivedFrom":[makeQuery(id+"Fb7tVVvyO8J0PkB_2.3.F13.boolean.opBoolean","MERGE",FACE,{"derivedFrom":[makeQuery(id+"Fb7tVVvyO8J0PkB_2.2.F13.boolean.opBoolean","MERGE",FACE,{"derivedFrom":[makeQuery(id+"Fb7tVVvyO8J0PkB_2.1.F13.boolean.opBoolean","MERGE",FACE,{"derivedFrom":[makeQuery(id+"F13.boolean.opBoolean","MERGE",FACE,{"derivedFrom":[makeQuery(id+"F11.opExtrude","CAP_FACE",FACE,{"disambiguationData":[OSD([sQuery(id+"F10.wireOp",EDGE,"E42"),sQuery(id+"F10.wireOp",EDGE,"E44")])],"isStart":true}),makeQuery(id+"F13.opExtrude","CAP_FACE",FACE,{"disambiguationData":[OSD([subQ2,subQ1,subQ0])],"isStart":true})]}),makeQuery(id+"Fb7tVVvyO8J0PkB_2.1.F13.opExtrude","CAP_FACE",FACE,{"disambiguationData":[OSD([subQ2,subQ1,subQ0])],"isStart":true})]}),makeQuery(id+"Fb7tVVvyO8J0PkB_2.2.F13.opExtrude","CAP_FACE",FACE,{"disambiguationData":[OSD([subQ2,subQ1,subQ0])],"isStart":true})]}),makeQuery(id+"Fb7tVVvyO8J0PkB_2.3.F13.opExtrude","CAP_FACE",FACE,{"disambiguationData":[OSD([subQ2,subQ1,subQ0])],"isStart":true})]}),makeQuery(id+"Fb7tVVvyO8J0PkB_2.4.F13.opExtrude","CAP_FACE",FACE,{"disambiguationData":[OSD([subQ2,subQ1,subQ0])],"isStart":true})]}),makeQuery(id+"Fb7tVVvyO8J0PkB_2.5.F13.opExtrude","CAP_FACE",FACE,{"disambiguationData":[OSD([subQ2,subQ1,subQ0])],"isStart":true})]}),makeQuery(id+"Fb7tVVvyO8J0PkB_2.6.F13.opExtrude","CAP_FACE",FACE,{"disambiguationData":[OSD([subQ2,subQ1,subQ0])],"isStart":true})]}),makeQuery(id+"Fb7tVVvyO8J0PkB_2.7.F13.opExtrude","CAP_FACE",FACE,{"disambiguationData":[OSD([subQ2,subQ1,subQ0])],"isStart":true})]}),makeQuery(id+"Fb7tVVvyO8J0PkB_2.8.F13.opExtrude","CAP_FACE",FACE,{"disambiguationData":[OSD([subQ2,subQ1,subQ0])],"isStart":true})]}),makeQuery(id+"Fb7tVVvyO8J0PkB_2.9.F13.opExtrude","CAP_FACE",FACE,{"disambiguationData":[OSD([subQ2,subQ1,subQ0])],"isStart":true})]}),makeQuery(id+"Fb7tVVvyO8J0PkB_2.10.F13.opExtrude","CAP_FACE",FACE,{"disambiguationData":[OSD([subQ2,subQ1,subQ0])],"isStart":true})]}),makeQuery(id+"Fb7tVVvyO8J0PkB_2.11.F13.opExtrude","CAP_FACE",FACE,{"disambiguationData":[OSD([subQ2,subQ1,subQ0])],"isStart":true})]}),makeQuery(id+"Fb7tVVvyO8J0PkB_2.12.F13.opExtrude","CAP_FACE",FACE,{"disambiguationData":[OSD([subQ2,subQ1,subQ0])],"isStart":true})]}),makeQuery(id+"Fb7tVVvyO8J0PkB_2.13.F13.opExtrude","CAP_FACE",FACE,{"disambiguationData":[OSD([subQ2,subQ1,subQ0])],"isStart":true})]}),makeQuery(id+"Fb7tVVvyO8J0PkB_2.14.F13.opExtrude","CAP_FACE",FACE,{"disambiguationData":[OSD([subQ2,subQ1,subQ0])],"isStart":true})]}),makeQuery(id+"Fb7tVVvyO8J0PkB_2.15.F13.opExtrude","CAP_FACE",FACE,{"disambiguationData":[OSD([subQ2,subQ1,subQ0])],"isStart":true})]}),makeQuery(id+"Fb7tVVvyO8J0PkB_2.16.F13.opExtrude","CAP_FACE",FACE,{"disambiguationData":[OSD([subQ2,subQ1,subQ0])],"isStart":true})]}),makeQuery(id+"Fb7tVVvyO8J0PkB_2.17.F13.opExtrude","CAP_FACE",FACE,{"disambiguationData":[OSD([subQ2,subQ1,subQ0])],"isStart":true})]}),makeQuery(id+"Fb7tVVvyO8J0PkB_2.18.F13.opExtrude","CAP_FACE",FACE,{"disambiguationData":[OSD([subQ2,subQ1,subQ0])],"isStart":true})]}),makeQuery(id+"Fb7tVVvyO8J0PkB_2.19.F13.opExtrude","CAP_FACE",FACE,{"disambiguationData":[OSD([subQ2,subQ1,subQ0])],"isStart":true})]}),makeQuery(id+"Fb7tVVvyO8J0PkB_2.20.F13.opExtrude","CAP_FACE",FACE,{"disambiguationData":[OSD([subQ2,subQ1,subQ0])],"isStart":true})]}),makeQuery(id+"Fb7tVVvyO8J0PkB_2.21.F13.opExtrude","CAP_FACE",FACE,{"disambiguationData":[OSD([subQ2,subQ1,subQ0])],"isStart":true})]}),makeQuery(id+"Fb7tVVvyO8J0PkB_2.22.F13.opExtrude","CAP_FACE",FACE,{"disambiguationData":[OSD([subQ2,subQ1,subQ0])],"isStart":true})]}),makeQuery(id+"Fb7tVVvyO8J0PkB_2.23.F13.opExtrude","CAP_FACE",FACE,{"disambiguationData":[OSD([subQ2,subQ1,subQ0])],"isStart":true})]}),makeQuery(id+"Fb7tVVvyO8J0PkB_2.24.F13.opExtrude","CAP_FACE",FACE,{"disambiguationData":[OSD([subQ2,subQ1,subQ0])],"isStart":true})]}),makeQuery(id+"Fb7tVVvyO8J0PkB_2.25.F13.opExtrude","CAP_FACE",FACE,{"disambiguationData":[OSD([subQ2,subQ1,subQ0])],"isStart":true})]}),makeQuery(id+"Fb7tVVvyO8J0PkB_2.26.F13.opExtrude","CAP_FACE",FACE,{"disambiguationData":[OSD([subQ2,subQ1,subQ0])],"isStart":true})]}),makeQuery(id+"Fb7tVVvyO8J0PkB_2.27.F13.opExtrude","CAP_FACE",FACE,{"disambiguationData":[OSD([subQ2,subQ1,subQ0])],"isStart":true})]}),makeQuery(id+"Fb7tVVvyO8J0PkB_2.28.F13.opExtrude","CAP_FACE",FACE,{"disambiguationData":[OSD([subQ2,subQ1,subQ0])],"isStart":true})]}),makeQuery(id+"Fb7tVVvyO8J0PkB_2.29.F13.opExtrude","CAP_FACE",FACE,{"disambiguationData":[OSD([subQ2,subQ1,subQ0])],"isStart":true})]}),makeQuery(id+"Fb7tVVvyO8J0PkB_2.30.F13.opExtrude","CAP_FACE",FACE,{"disambiguationData":[OSD([subQ2,subQ1,subQ0])],"isStart":true})]}),makeQuery(id+"Fb7tVVvyO8J0PkB_2.31.F13.opExtrude","CAP_FACE",FACE,{"disambiguationData":[OSD([subQ2,subQ1,subQ0])],"isStart":true})]}),makeQuery(id+"Fb7tVVvyO8J0PkB_2.32.F13.opExtrude","CAP_FACE",FACE,{"disambiguationData":[OSD([subQ2,subQ1,subQ0])],"isStart":true})]}),makeQuery(id+"Fb7tVVvyO8J0PkB_2.33.F13.opExtrude","CAP_FACE",FACE,{"disambiguationData":[OSD([subQ2,subQ1,subQ0])],"isStart":true})]}),makeQuery(id+"Fb7tVVvyO8J0PkB_2.34.F13.opExtrude","CAP_FACE",FACE,{"disambiguationData":[OSD([subQ2,subQ1,subQ0])],"isStart":true})]}),makeQuery(id+"Fb7tVVvyO8J0PkB_2.35.F13.opExtrude","CAP_FACE",FACE,{"disambiguationData":[OSD([subQ2,subQ1,subQ0])],"isStart":true})]}),makeQuery(id+"F16.opExtrude","CAP_FACE",FACE,{"disambiguationData":[OSD([sQuery(id+"F15.wireOp",EDGE,"uEIJswN8-hliM-NGML-rBW8-biOoMusq29Py"),sQuery(id+"F15.wireOp",EDGE,"E51"),sQuery(id+"F15.wireOp",EDGE,"E52"),sQuery(id+"F15.wireOp",EDGE,"RIxkjdCn-LYEG-4k8K-00l7-vMFKRM702DAv"),sQuery(id+"F15.wireOp",EDGE,"b80e2d38-e699-45d1-b1d6-f63e524835e6"),sQuery(id+"F15.wireOp",EDGE,"5b5d3a2e-1ab0-4b8c-b053-a8e82fd700e5")])],"isStart":true})]});}
            mirror(context, id + "F24", {"operationType" : NewBodyOperationType.ADD, "entities" : qUnion([Q0]), "mirrorPlane" : qUnion([Q1])});
        }
        {
            var Q0;
            {var subQ0=makeQuery(id+"F16.opExtrude","SWEPT_EDGE",EDGE,{"disambiguationData":[OSD([sQuery(id+"F15.wireOp",EDGE,"E55"),sQuery(id+"F15.wireOp",EDGE,"E56")])]});Q0=makeQuery(id+"F24.boolean.opBoolean","MERGE",EDGE,{"derivedFrom":[subQ0,makeQuery(id+"F24.opPattern","COPY",EDGE,{"derivedFrom":subQ0,"instanceName":"1"})]});}
            var Q1;
            {var subQ0=makeQuery(id+"F16.opExtrude","SWEPT_EDGE",EDGE,{"disambiguationData":[OSD([sQuery(id+"F15.wireOp",EDGE,"E54"),sQuery(id+"F15.wireOp",EDGE,"E55")])]});Q1=makeQuery(id+"F24.boolean.opBoolean","MERGE",EDGE,{"derivedFrom":[subQ0,makeQuery(id+"F24.opPattern","COPY",EDGE,{"derivedFrom":subQ0,"instanceName":"1"})]});}
            fillet(context, id + "F25", {"entities" : qUnion([Q0, Q1]), "radius" : 1.2 * mm, "tangentPropagation" : true, "rho" : .6, "crossSection" : FilletCrossSection.CONIC, "allowEdgeOverflow" : false});
        }
    });
